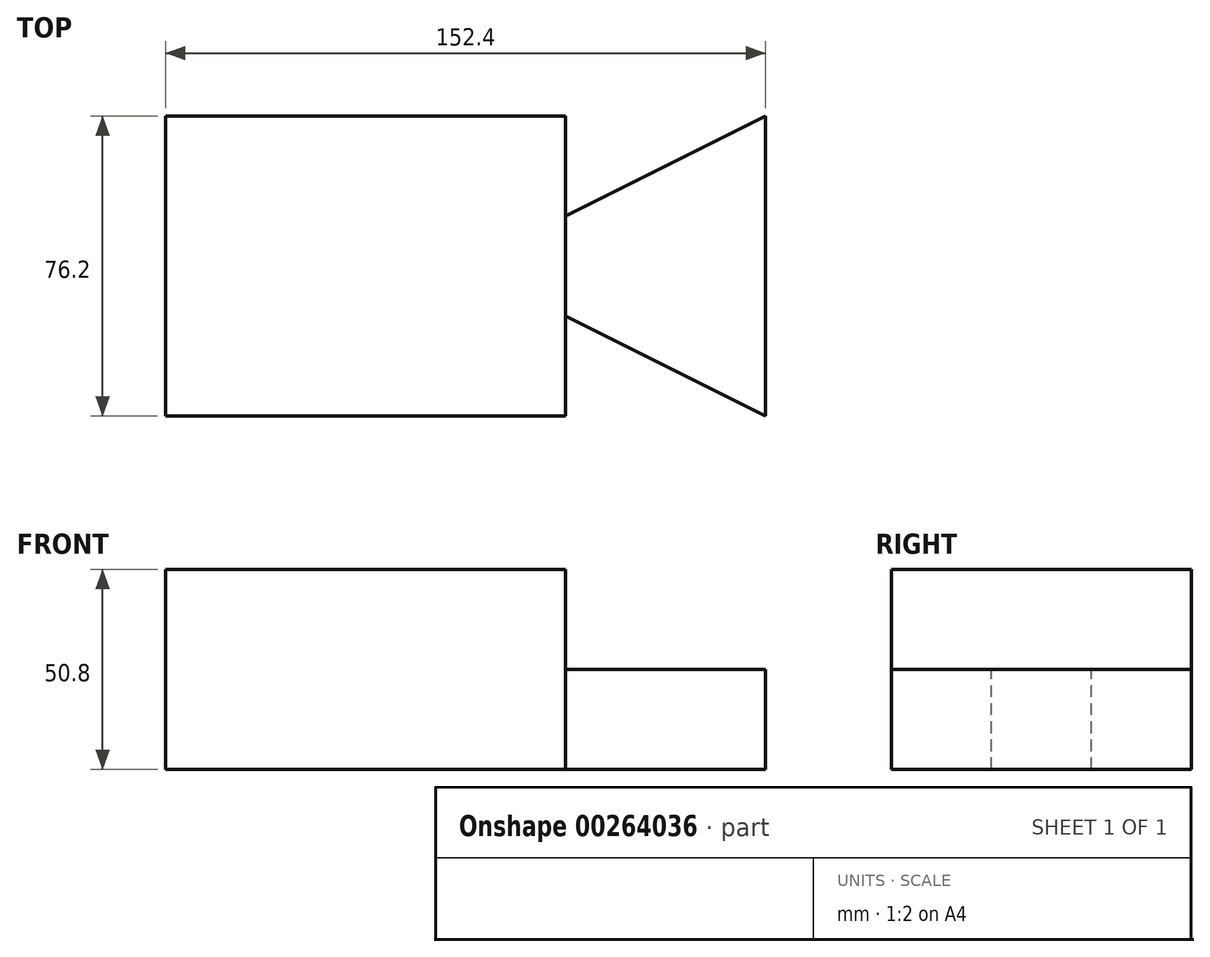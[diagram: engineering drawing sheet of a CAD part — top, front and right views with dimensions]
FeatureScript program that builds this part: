
annotation { "Feature Type Name" : "Feature", "Feature Type Description" : "" }
export const myFeature = defineFeature(function(context is Context, id is Id, definition is map)
    precondition{}
    {
        {
            var Q0;
            Q0=qCreatedBy(makeId("Front.planeOp"),FACE);
            var sketch = newSketch(context, id + "F0", { "sketchPlane" : qUnion([Q0])});
            skLineSegment(sketch, "E0.bottom", {"start": v(-66.38, 25.4) * mm, "end": v(35.22, 25.4) * mm});
            skLineSegment(sketch, "E0.top", {"start": v(-66.38, -25.4) * mm, "end": v(35.22, -25.4) * mm});
            skLineSegment(sketch, "E0.left", {"start": v(-66.38, 25.4) * mm, "end": v(-66.38, -25.4) * mm});
            skLineSegment(sketch, "E0.right", {"start": v(35.22, 25.4) * mm, "end": v(35.22, -25.4) * mm});
            skLineSegment(sketch, "E1.bottom", {"start": v(35.22, -25.4) * mm, "end": v(86.02, -25.4) * mm});
            skLineSegment(sketch, "E1.top", {"start": v(35.22, 0) * mm, "end": v(86.02, 0) * mm});
            skLineSegment(sketch, "E1.left", {"start": v(35.22, -25.4) * mm, "end": v(35.22, 0) * mm});
            skLineSegment(sketch, "E1.right", {"start": v(86.02, -25.4) * mm, "end": v(86.02, 0) * mm});
            skSolve(sketch);
        }
        {
            var Q0;
            Q0=makeQuery(id+"F0.imprint","IMPRINT",FACE,{"disambiguationData":[TD([[makeQuery(id+"F0.imprint","IMPRINT",EDGE,{"derivedFrom":sQuery(id+"F0.wireOp",EDGE,"E0.bottom")}),-1.0]])]});
            var Q1;
            Q1=makeQuery(id+"F0.imprint","IMPRINT",FACE,{"disambiguationData":[TD([[makeQuery(id+"F0.imprint","IMPRINT",EDGE,{"derivedFrom":sQuery(id+"F0.wireOp",EDGE,"E1.bottom")}),1.0]])]});
            extrude(context, id + "F1", {"entities" : qUnion([Q0, Q1]), "depth" : 38.1 * mm});
        }
        {
            var Q0;
            Q0=makeQuery(id+"F1.opExtrude","CAP_FACE",FACE,{"disambiguationData":[OSD([sQuery(id+"F0.wireOp",EDGE,"E0.bottom"),sQuery(id+"F0.wireOp",EDGE,"E0.top"),sQuery(id+"F0.wireOp",EDGE,"E0.left"),sQuery(id+"F0.wireOp",EDGE,"E0.right"),sQuery(id+"F0.wireOp",EDGE,"E1.bottom"),sQuery(id+"F0.wireOp",EDGE,"E1.top"),sQuery(id+"F0.wireOp",EDGE,"E1.right")])],"isStart":true});
            extrude(context, id + "F2", {"entities" : qUnion([Q0]), "operationType" : NewBodyOperationType.ADD, "depth" : 38.1 * mm});
        }
        {
            var Q0;
            {var subQ0=sQuery(id+"F0.wireOp",EDGE,"E1.top");Q0=makeQuery(id+"F2.boolean.opBoolean","MERGE",FACE,{"derivedFrom":[makeQuery(id+"F1.opExtrude","SWEPT_FACE",FACE,{"disambiguationData":[OSD([subQ0])]}),makeQuery(id+"F2.opExtrude","SWEPT_FACE",FACE,{"disambiguationData":[OSD([subQ0])]})]});}
            var sketch = newSketch(context, id + "F3", { "sketchPlane" : qUnion([Q0])});
            skLineSegment(sketch, "E2", {"start": v(86.02, -38.1) * mm, "end": v(35.22, -38.1) * mm});
            skLineSegment(sketch, "E3", {"start": v(35.22, -38.1) * mm, "end": v(35.22, -12.7) * mm});
            skLineSegment(sketch, "E4", {"start": v(35.22, -12.7) * mm, "end": v(86.02, -38.1) * mm});
            skLineSegment(sketch, "E5", {"start": v(86.02, 38.1) * mm, "end": v(35.22, 38.1) * mm});
            skLineSegment(sketch, "E6", {"start": v(35.22, 38.1) * mm, "end": v(35.22, 12.7) * mm});
            skLineSegment(sketch, "E7", {"start": v(35.22, 12.7) * mm, "end": v(86.02, 38.1) * mm});
            skSolve(sketch);
        }
        {
            var Q0;
            Q0=makeQuery(id+"F3.imprint","IMPRINT",FACE,{"disambiguationData":[TD([[makeQuery(id+"F3.imprint","IMPRINT",EDGE,{"derivedFrom":sQuery(id+"F3.wireOp",EDGE,"E2")}),1.0]])]});
            var Q1;
            Q1=makeQuery(id+"F3.imprint","IMPRINT",FACE,{"disambiguationData":[TD([[makeQuery(id+"F3.imprint","IMPRINT",EDGE,{"derivedFrom":sQuery(id+"F3.wireOp",EDGE,"E5")}),-1.0]])]});
            extrude(context, id + "F4", {"entities" : qUnion([Q0, Q1]), "operationType" : NewBodyOperationType.REMOVE, "oppositeDirection" : true, "depth" : 25.4 * mm});
        }
    });
